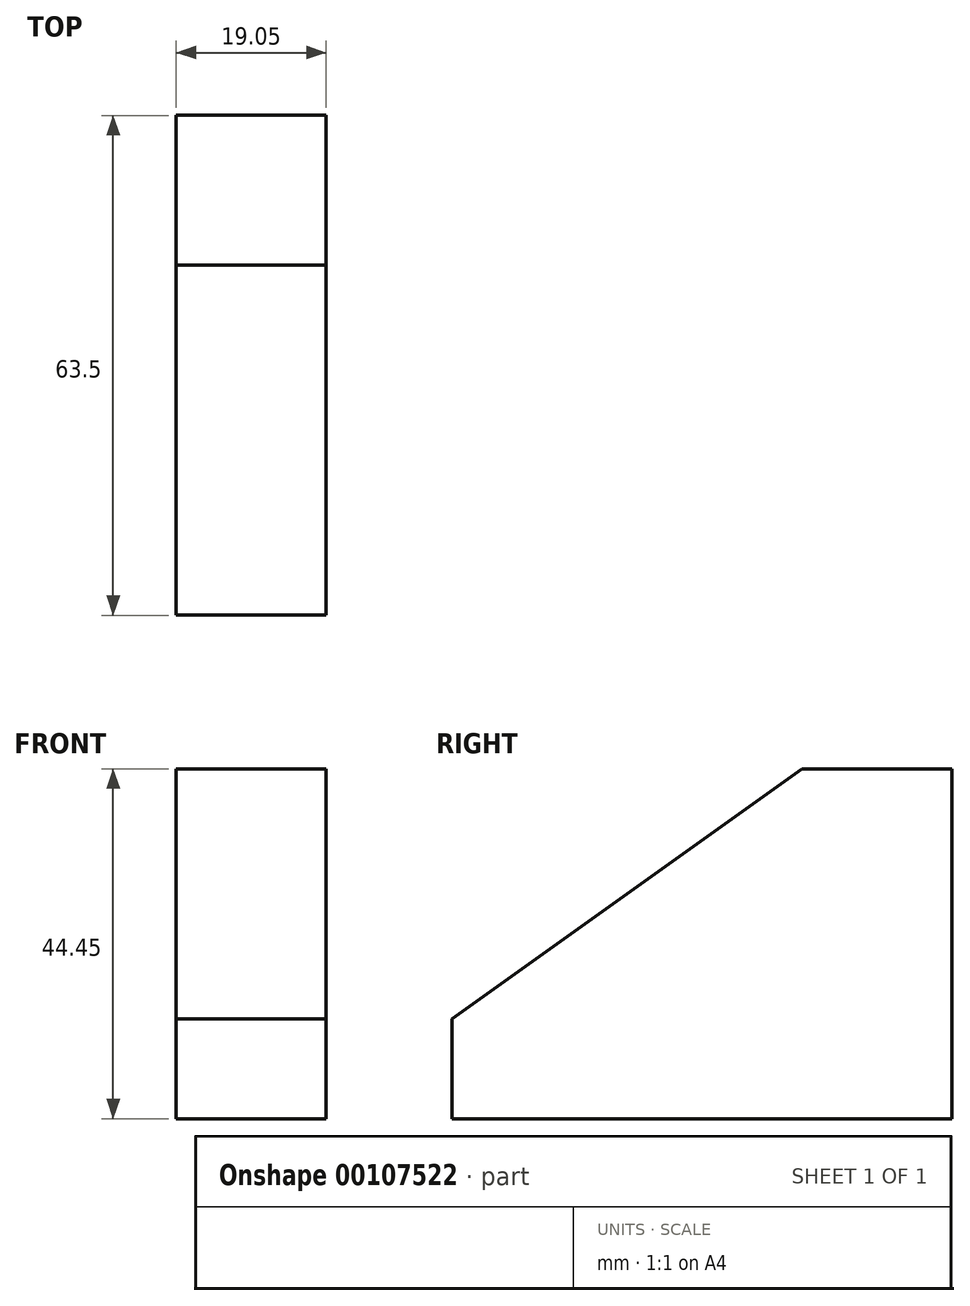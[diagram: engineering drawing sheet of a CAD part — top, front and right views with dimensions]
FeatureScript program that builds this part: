
annotation { "Feature Type Name" : "Feature", "Feature Type Description" : "" }
export const myFeature = defineFeature(function(context is Context, id is Id, definition is map)
    precondition{}
    {
        {
            var Q0;
            Q0=qCreatedBy(makeId("Right.planeOp"),FACE);
            var sketch = newSketch(context, id + "F0", { "sketchPlane" : qUnion([Q0])});
            skLineSegment(sketch, "E0", {"start": v(-33.86, -12.38) * mm, "end": v(-33.86, -25.08) * mm});
            skLineSegment(sketch, "E1", {"start": v(-33.86, -25.08) * mm, "end": v(29.64, -25.08) * mm});
            skLineSegment(sketch, "E2", {"start": v(29.64, -25.08) * mm, "end": v(29.64, 19.37) * mm});
            skLineSegment(sketch, "E3", {"start": v(29.64, 19.37) * mm, "end": v(10.6, 19.37) * mm});
            skLineSegment(sketch, "E4", {"start": v(10.6, 19.37) * mm, "end": v(-33.86, -12.38) * mm});
            skSolve(sketch);
        }
        {
            var Q0;
            Q0=makeQuery(id+"F0.imprint","IMPRINT",FACE,{"disambiguationData":[TD([[makeQuery(id+"F0.imprint","IMPRINT",EDGE,{"derivedFrom":sQuery(id+"F0.wireOp",EDGE,"E0")}),1.0]])]});
            extrude(context, id + "F1", {"entities" : qUnion([Q0]), "depth" : 19.05 * mm});
        }
    });
